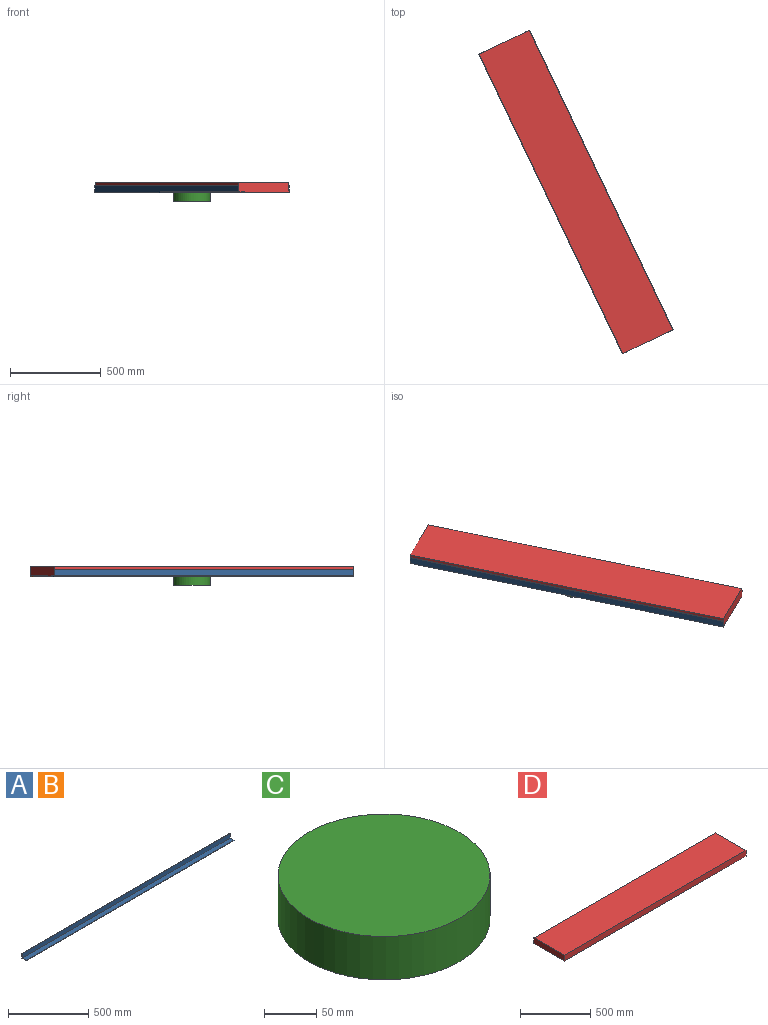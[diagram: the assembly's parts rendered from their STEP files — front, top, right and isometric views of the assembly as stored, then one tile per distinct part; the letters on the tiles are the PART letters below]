
ASSEMBLY  parts=4 mates=3
PART A: 8 faces, bbox 1828.8x38.1x38.1 mm
  f0: plane 1828.8x34.93mm, normal (0,-1,0), area 63870.8mm2, adj f1,f5,f6,f7
  f1: plane 1828.8x34.93mm, normal (0,0,1), area 63870.8mm2, adj f0,f2,f6,f7
  f2: plane 1828.8x3.18mm, normal (0,-1,0), area 5806.4mm2, adj f1,f3,f6,f7
  f3: plane 1828.8x38.1mm, normal (0,0,-1), area 69677.3mm2, adj f2,f4,f6,f7
  f4: plane 1828.8x38.1mm, normal (0,1,0), area 69677.3mm2, adj f3,f5,f6,f7
  f5: plane 1828.8x3.18mm, normal (0,0,1), area 5806.4mm2, adj f0,f4,f6,f7
  f6: plane 38.1x38.1mm, normal (1,0,0), area 231.9mm2, adj f0,f1,f2,f3,f4,f5
  f7: plane 38.1x38.1mm, normal (-1,0,0), area 231.9mm2, adj f0,f1,f2,f3,f4,f5
PART B: same geometry as A
PART C: 3 faces, bbox 203.2x203.2x50.8 mm
  f0: cylinder r=101.6mm len=203.2mm, axis (0,0,-1), area 32429.3mm2, adj f1,f2
  f1: plane 203.2x203.2mm, normal (0,0,1), area 32429.3mm2, adj f0
  f2: plane 203.2x203.2mm, normal (0,0,-1), area 32429.3mm2, adj f0
PART D: 6 faces, bbox 1828.8x304.8x50.8 mm
  f0: plane 304.8x50.8mm, normal (-1,0,0), area 15483.8mm2, adj f1,f3,f4,f5
  f1: plane 1828.8x50.8mm, normal (0,-1,0), area 92903mm2, adj f0,f2,f4,f5
  f2: plane 304.8x50.8mm, normal (1,0,0), area 15483.8mm2, adj f1,f3,f4,f5
  f3: plane 1828.8x50.8mm, normal (0,1,0), area 92903mm2, adj f0,f2,f4,f5
  f4: plane 1828.8x304.8mm, normal (0,0,1), area 557418.2mm2, adj f0,f1,f2,f3
  f5: plane 1828.8x304.8mm, normal (0,0,-1), area 557418.2mm2, adj f0,f1,f2,f3
PLACE A rot(axis=(0,0,1),115.6deg) t=(314.57,-702.56,6.14)mm
PLACE B rot(axis=(-0.41,-0.65,0.65),135.7deg) t=(366.81,-677.53,197.89)mm
PLACE C rot(axis=(1,0,0),0deg) t=(-140.86,93.17,-72.23)mm fixed
PLACE D rot(axis=(0,0,1),115.6deg) t=(-192.37,326.58,-21.43)mm
MATE fastened D.f2 <-> B.f6  axis (-0.43,0.9,0) through (-398.51,983.66,-21.43)mm
MATE revolute C.f0 <-> D.f5  axis (0,0,1) through (-140.86,93.17,-21.43)mm
MATE fastened A.f6 <-> D.f2  axis (-0.43,0.9,0) through (-673.39,851.96,-21.43)mm
